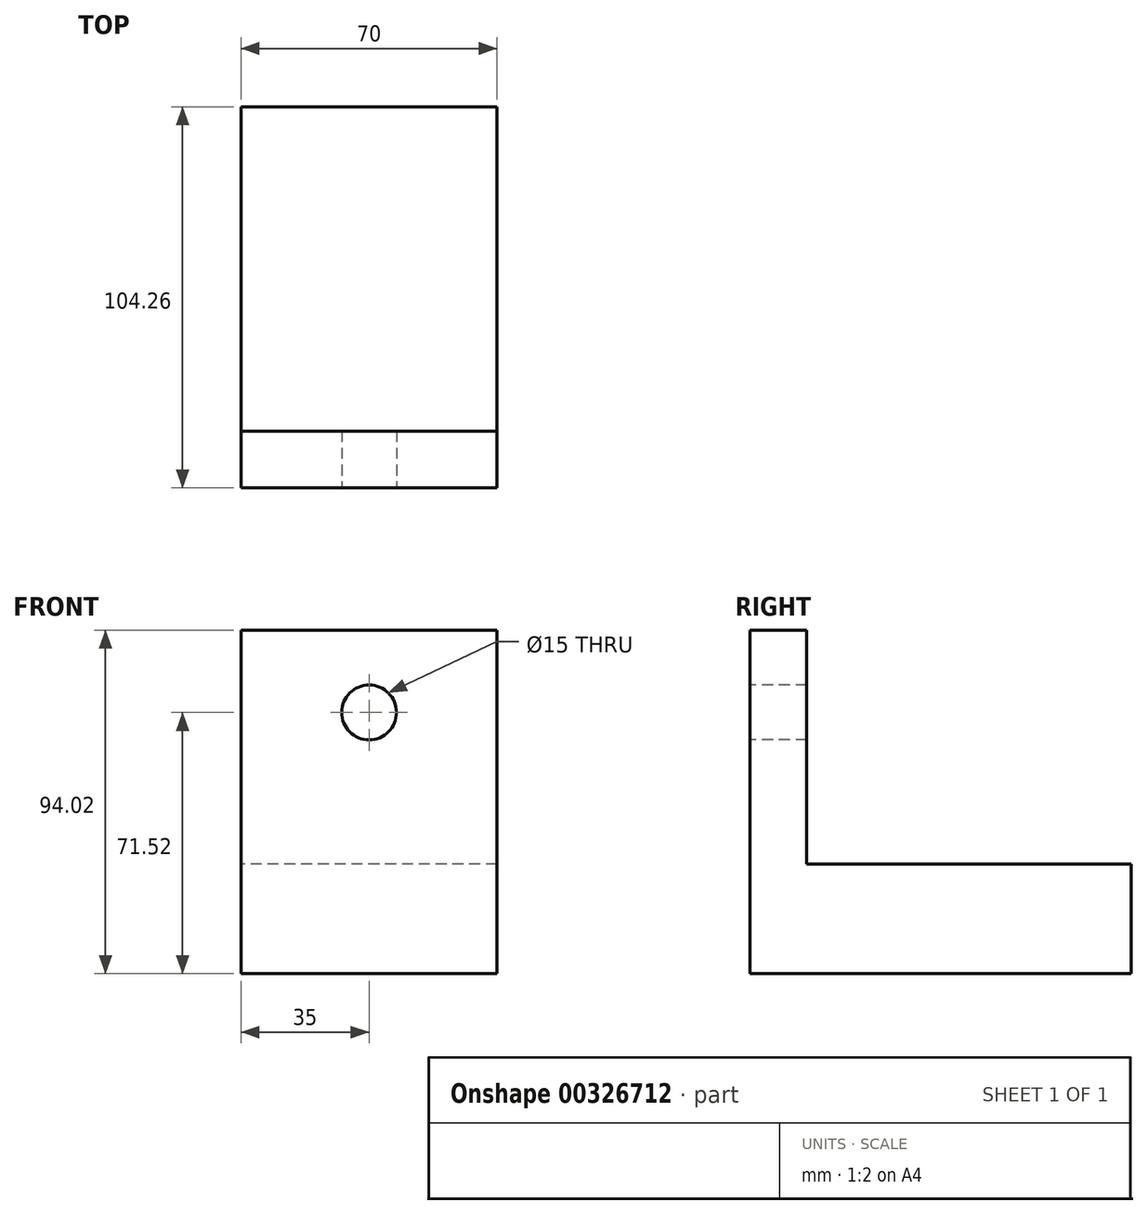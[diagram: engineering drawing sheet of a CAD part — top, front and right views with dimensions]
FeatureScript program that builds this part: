
annotation { "Feature Type Name" : "Feature", "Feature Type Description" : "" }
export const myFeature = defineFeature(function(context is Context, id is Id, definition is map)
    precondition{}
    {
        {
            var Q0;
            Q0=qCreatedBy(makeId("Right.planeOp"),FACE);
            var sketch = newSketch(context, id + "F0", { "sketchPlane" : qUnion([Q0])});
            skLineSegment(sketch, "E0.bottom", {"start": v(0, 0) * mm, "end": v(15.53, 0) * mm});
            skLineSegment(sketch, "E0.top", {"start": v(0, 94.02) * mm, "end": v(15.53, 94.02) * mm});
            skLineSegment(sketch, "E0.left", {"start": v(0, 0) * mm, "end": v(0, 94.02) * mm});
            skLineSegment(sketch, "E0.right", {"start": v(15.53, 0) * mm, "end": v(15.53, 94.02) * mm});
            skLineSegment(sketch, "E1.bottom", {"start": v(15.53, 0) * mm, "end": v(104.26, 0) * mm});
            skLineSegment(sketch, "E1.top", {"start": v(15.53, 30) * mm, "end": v(104.26, 30) * mm});
            skLineSegment(sketch, "E1.left", {"start": v(15.53, 0) * mm, "end": v(15.53, 30) * mm});
            skLineSegment(sketch, "E1.right", {"start": v(104.26, 0) * mm, "end": v(104.26, 30) * mm});
            skSolve(sketch);
        }
        {
            var Q0;
            Q0=makeQuery(id+"F0.imprint","IMPRINT",FACE,{"disambiguationData":[TD([[makeQuery(id+"F0.imprint","IMPRINT",EDGE,{"derivedFrom":sQuery(id+"F0.wireOp",EDGE,"E1.bottom")}),1.0]])]});
            var Q1;
            Q1=makeQuery(id+"F0.imprint","IMPRINT",FACE,{"disambiguationData":[TD([[makeQuery(id+"F0.imprint","IMPRINT",EDGE,{"derivedFrom":sQuery(id+"F0.wireOp",EDGE,"E0.bottom")}),1.0]])]});
            extrude(context, id + "F1", {"entities" : qUnion([Q0, Q1]), "depth" : 70 * mm});
        }
        {
            var Q0;
            Q0=makeQuery(id+"F1.opExtrude","SWEPT_FACE",FACE,{"disambiguationData":[OSD([sQuery(id+"F0.wireOp",EDGE,"E0.left")])]});
            var sketch = newSketch(context, id + "F2", { "sketchPlane" : qUnion([Q0])});
            skLineSegment(sketch, "E2", {"start": v(22.76, 94.02) * mm, "end": v(0, 72.21) * mm});
            skLineSegment(sketch, "E3", {"start": v(35, 119.26) * mm, "end": v(35, 139.2) * mm, "construction": true});
            skPoint(sketch, "E3.startSnap0", {"position": v(35, 94.02) * mm});
            skLineSegment(sketch, "E4.MirrorCS", {"start": v(47.24, 94.02) * mm, "end": v(70, 72.21) * mm});
            skLineSegment(sketch, "E5", {"start": v(22.76, 94.02) * mm, "end": v(47.24, 94.02) * mm});
            skLineSegment(sketch, "E6", {"start": v(0, 72.21) * mm, "end": v(0, 0) * mm});
            skLineSegment(sketch, "E7", {"start": v(0, 0) * mm, "end": v(70, 0) * mm});
            skLineSegment(sketch, "E8", {"start": v(70, 0) * mm, "end": v(70, 69.97) * mm});
            skCircle(sketch, "E9", {"center": v(35, 71.52) * mm, "radius": 7.5 * mm});
            skPoint(sketch, "E10", {"position": v(35, 79.02) * mm});
            skSolve(sketch);
        }
        {
            var Q0;
            Q0=makeQuery(id+"F2.imprint","IMPRINT",FACE,{"disambiguationData":[TD([[makeQuery(id+"F2.imprint","IMPRINT",EDGE,{"derivedFrom":sQuery(id+"F2.wireOp",EDGE,"E9")}),1.0]])]});
            var Q1;
            Q1=sQuery(id+"F2.wireOp",EDGE,"E9");
            extrude(context, id + "F3", {"entities" : qUnion([Q0]), "operationType" : NewBodyOperationType.REMOVE, "surfaceEntities" : qUnion([Q1]), "oppositeDirection" : true, "depth" : 25 * mm});
        }
    });
